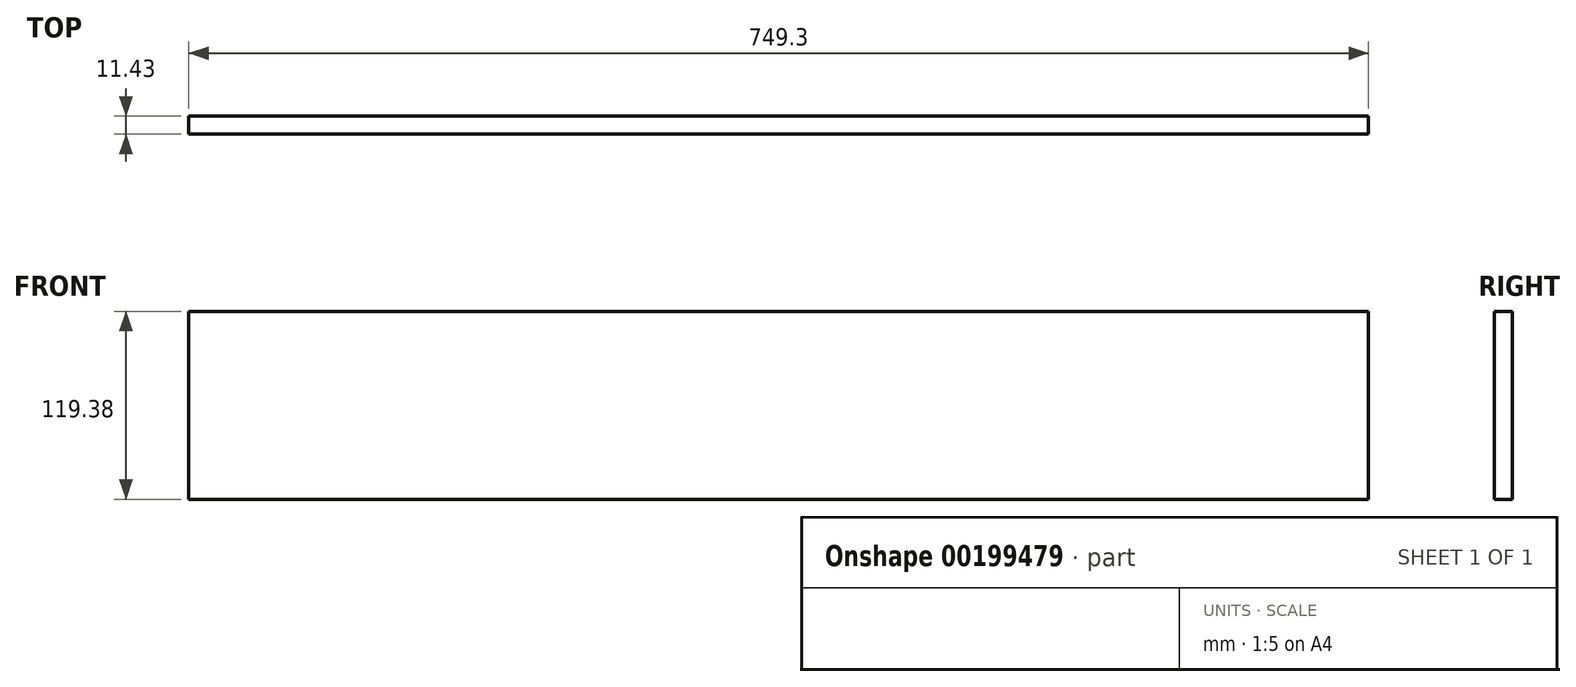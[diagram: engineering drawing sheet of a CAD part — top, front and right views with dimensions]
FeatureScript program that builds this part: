
annotation { "Feature Type Name" : "Feature", "Feature Type Description" : "" }
export const myFeature = defineFeature(function(context is Context, id is Id, definition is map)
    precondition{}
    {
        {
            var Q0;
            Q0=qCreatedBy(makeId("Front.planeOp"),FACE);
            var sketch = newSketch(context, id + "F0", { "sketchPlane" : qUnion([Q0])});
            skLineSegment(sketch, "E0.bottom", {"start": v(-383.18, 48.2) * mm, "end": v(366.12, 48.2) * mm});
            skLineSegment(sketch, "E0.top", {"start": v(-383.18, -71.17) * mm, "end": v(366.12, -71.17) * mm});
            skLineSegment(sketch, "E0.left", {"start": v(-383.18, 48.2) * mm, "end": v(-383.18, -71.17) * mm});
            skLineSegment(sketch, "E0.right", {"start": v(366.12, 48.2) * mm, "end": v(366.12, -71.17) * mm});
            skSolve(sketch);
        }
        {
            var Q0;
            Q0 = qSketchRegion(id + "F0", true);
            extrude(context, id + "F1", {"entities" : qUnion([Q0]), "depth" : 11.43 * mm});
        }
    });
